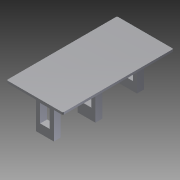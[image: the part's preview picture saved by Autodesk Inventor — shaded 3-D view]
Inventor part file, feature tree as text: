
AUTODESK INVENTOR PART (.ipt)
format: ipt  version: 2014 (Build 180170000, 170)  size: 124,416 bytes
history: native  units: in
note: dims shown in document units (in); Inventor stores cm internally (conversion verified against a paired STEP export)
features: other x7, extrude x3, sketch x3, pattern_linear x1
ambient origin geometry x8: Origin, YZ Plane, XZ Plane, XY Plane, X Axis, Y Axis, Z Axis, Center Point
bodies: Solid1 (feature_tree)
feature tree (14):
  extrude  "Extrusion1"  Depth=0.031in TaperAngle=0.0deg
  extrude  "Extrusion2"  Depth=0.031in TaperAngle=0.0deg
  pattern_linear  "Rectangular Pattern1"  [2 undecoded]
  extrude  "Extrusion3"  [1 undecoded]
  other  "to_base_XY"
  other  "to_base_YZ"
  other  "to_base_ZX"
  other  "to_base_X"
  other  "to_base_Y"
  other  "to_base_Z"
  other  "to_base_Center"
  sketch  "Sketch_2"  dims[d4=0.7874in d6=0.37in d7=0.3937in d9=0.0in d10=0.031in d11=0.0in]
  sketch  "Sketch_1"  dims[d0=0.01in d1=0.0in d2=0.031in d3=0.0in]
  sketch  "Sketch_14"
note: 3 required parameter values undecoded (feature->parameter linkage not recoverable at this tier; creation-order binding heuristic only, values carry confidence <= 0.55)
